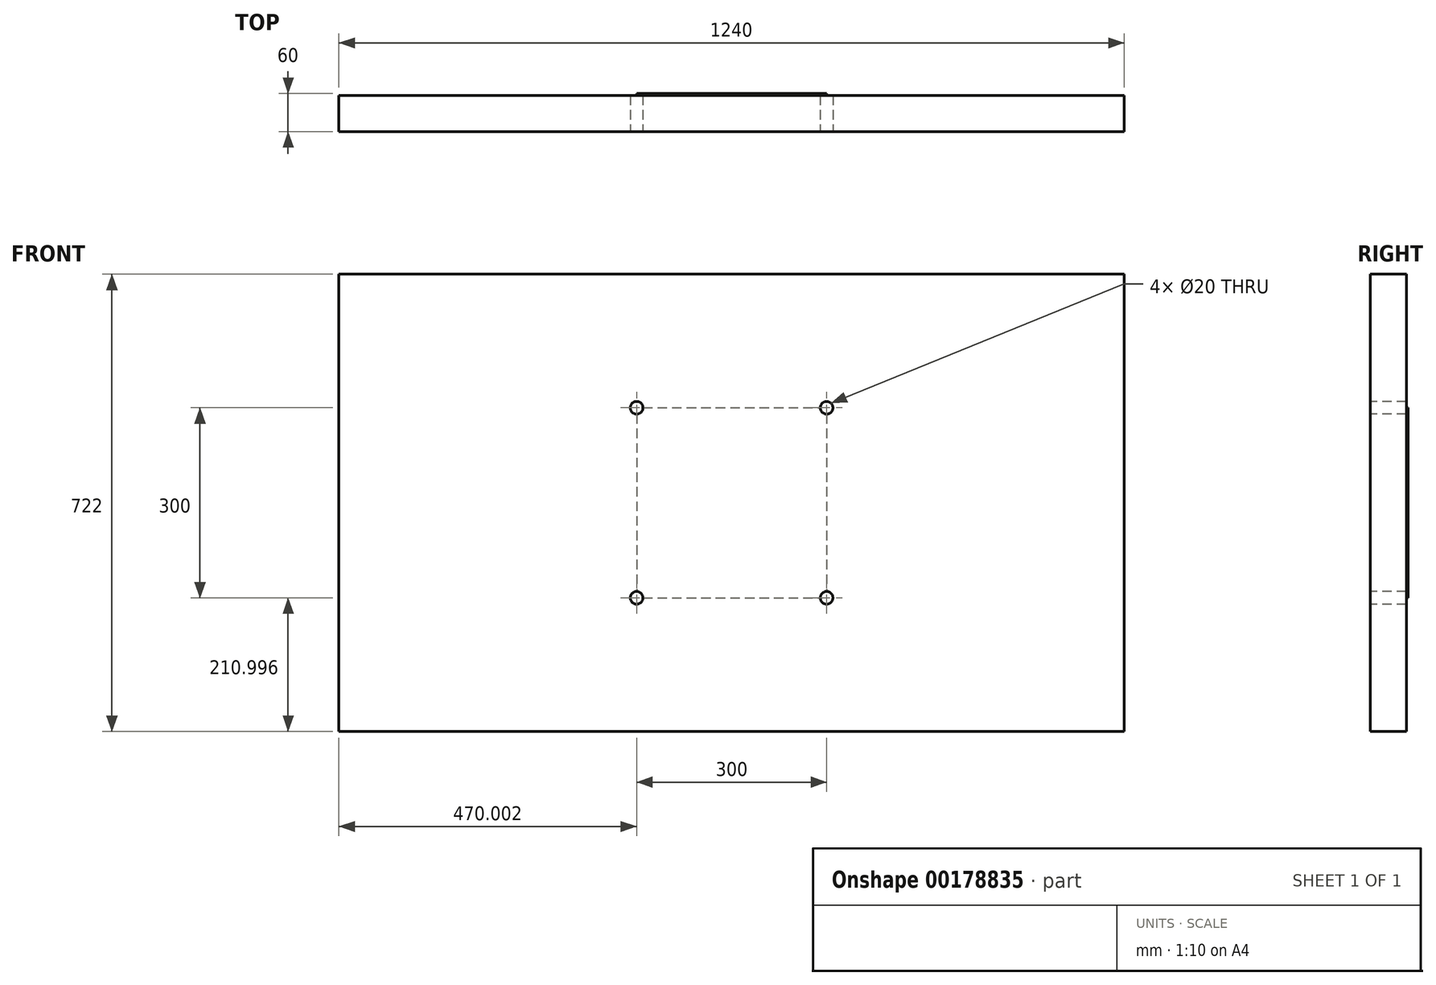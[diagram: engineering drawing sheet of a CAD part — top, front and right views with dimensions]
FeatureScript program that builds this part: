
annotation { "Feature Type Name" : "Feature", "Feature Type Description" : "" }
export const myFeature = defineFeature(function(context is Context, id is Id, definition is map)
    precondition{}
    {
        {
            var Q0;
            Q0=qCreatedBy(makeId("Front.planeOp"),FACE);
            var sketch = newSketch(context, id + "F0", { "sketchPlane" : qUnion([Q0])});
            skLineSegment(sketch, "E0.bottom", {"start": v(-589.74, 398.92) * mm, "end": v(650.26, 398.92) * mm});
            skLineSegment(sketch, "E0.top", {"start": v(-589.74, -323.08) * mm, "end": v(650.26, -323.08) * mm});
            skLineSegment(sketch, "E0.left", {"start": v(-589.74, 398.92) * mm, "end": v(-589.74, -323.08) * mm});
            skLineSegment(sketch, "E0.right", {"start": v(650.26, 398.92) * mm, "end": v(650.26, -323.08) * mm});
            skLineSegment(sketch, "E1.bottom", {"start": v(-119.74, 187.92) * mm, "end": v(180.26, 187.92) * mm});
            skLineSegment(sketch, "E1.top", {"start": v(-119.74, -112.08) * mm, "end": v(180.26, -112.08) * mm});
            skLineSegment(sketch, "E1.left", {"start": v(-119.74, 187.92) * mm, "end": v(-119.74, -112.08) * mm});
            skLineSegment(sketch, "E1.right", {"start": v(180.26, 187.92) * mm, "end": v(180.26, -112.08) * mm});
            skCircle(sketch, "E2", {"center": v(180.26, -112.08) * mm, "radius": 10 * mm});
            skCircle(sketch, "E3", {"center": v(-119.74, -112.08) * mm, "radius": 10 * mm});
            skCircle(sketch, "E4", {"center": v(-119.74, 187.92) * mm, "radius": 10 * mm});
            skCircle(sketch, "E5", {"center": v(180.26, 187.92) * mm, "radius": 10 * mm});
            skSolve(sketch);
        }
        {
            var Q0;
            Q0=makeQuery(id+"F0.imprint","IMPRINT",FACE,{"disambiguationData":[TD([[makeQuery(id+"F0.imprint","IMPRINT",EDGE,{"derivedFrom":sQuery(id+"F0.wireOp",EDGE,"E0.bottom")}),-1.0]])]});
            extrude(context, id + "F1", {"entities" : qUnion([Q0]), "oppositeDirection" : true, "depth" : 57 * mm});
        }
        {
            var Q0;
            {var subQ10=sQuery(id+"F0.wireOp",EDGE,"E4");var subQ13=sQuery(id+"F0.wireOp",EDGE,"E1.bottom");var subQ14=makeQuery(id+"F0.imprint","INTERSECT",VERTEX,{"derivedFrom":[subQ13,subQ10]});Q0=makeQuery(id+"F0.imprint","IMPRINT",FACE,{"disambiguationData":[TD([[makeQuery(id+"F0.imprint","IMPRINT",EDGE,{"disambiguationData":[TD([[subQ14,-1.0]])],"derivedFrom":subQ13}),-1.0]])]});}
            extrude(context, id + "F2", {"entities" : qUnion([Q0]), "operationType" : NewBodyOperationType.ADD, "oppositeDirection" : true, "depth" : 60 * mm});
        }
    });
